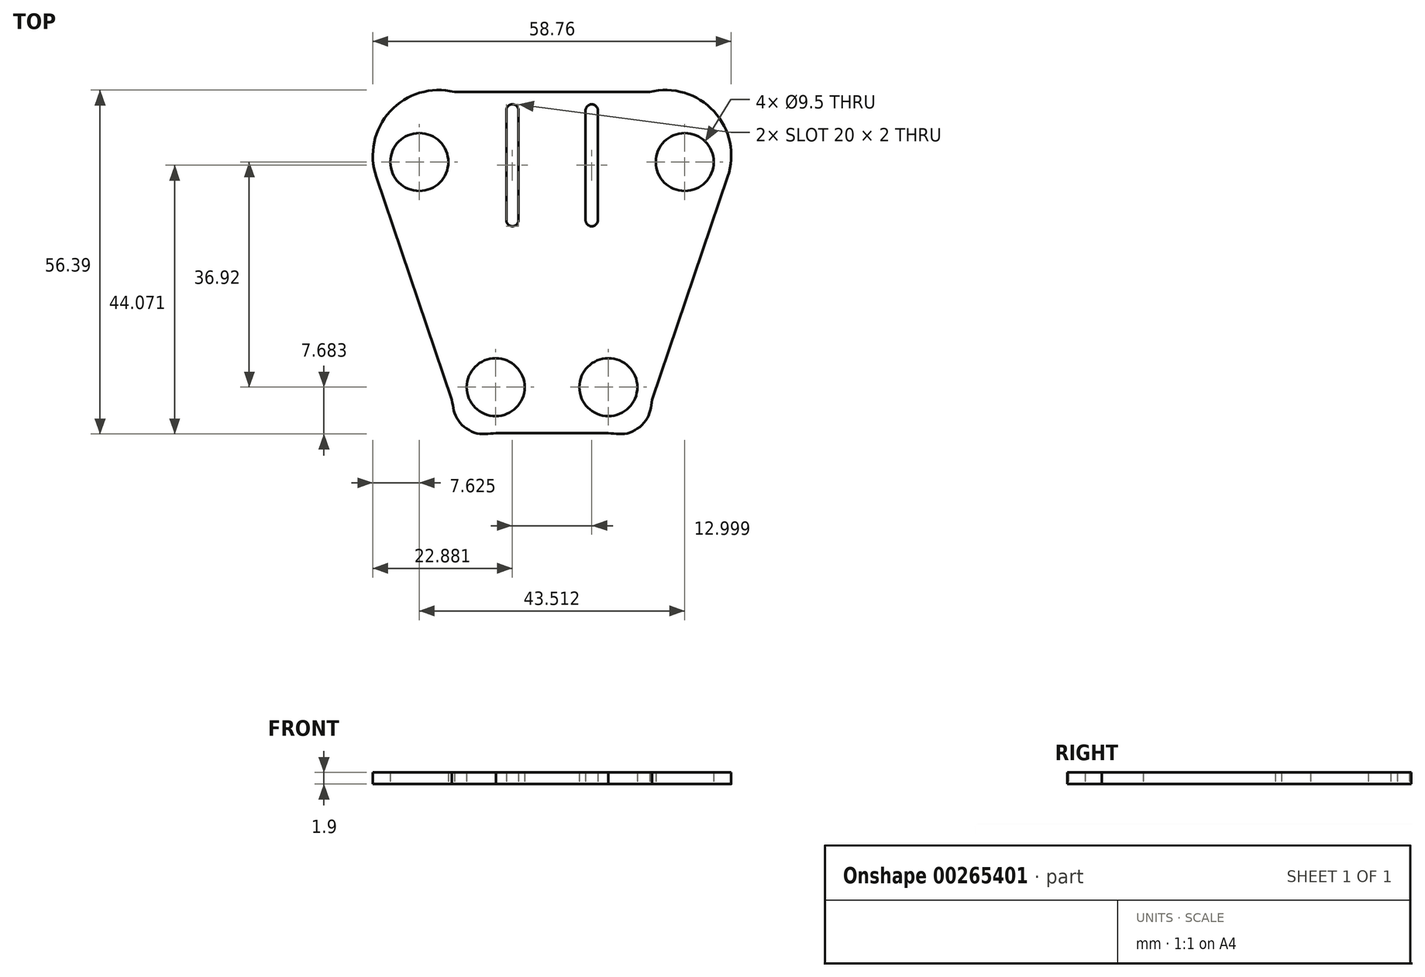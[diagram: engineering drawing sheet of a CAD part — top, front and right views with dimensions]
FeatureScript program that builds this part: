
annotation { "Feature Type Name" : "Feature", "Feature Type Description" : "" }
export const myFeature = defineFeature(function(context is Context, id is Id, definition is map)
    precondition{}
    {
        {
            var Q0;
            Q0=qCreatedBy(makeId("Top.planeOp"),FACE);
            var sketch = newSketch(context, id + "F0", { "sketchPlane" : qUnion([Q0])});
            skEllipse(sketch, "E0", {"center": v(22.76, 23.7) * mm, "majorRadius": 4.75 * mm, "minorRadius": 4.75 * mm, "majorAxis": v(1, 0)});
            skEllipse(sketch, "E1", {"center": v(10.24, -13.22) * mm, "majorRadius": 4.75 * mm, "minorRadius": 4.75 * mm, "majorAxis": v(1, 0)});
            skFitSpline(sketch, "E2", {"points": [v(10.2, -20.72) * mm, v(13.54, -20.72) * mm, v(16.48, -18.5) * mm, v(17.4, -15.28) * mm]});
            skArc(sketch, "E3", {"start": v(29.8, 21.26) * mm, "mid": v(29.86, 21.4) * mm, "end": v(29.9, 21.54) * mm});
            skLineSegment(sketch, "E4", {"start": v(17.4, -15.28) * mm, "end": v(29.8, 21.26) * mm});
            skLineSegment(sketch, "E5", {"start": v(1, -36.13) * mm, "end": v(1, 35.17) * mm, "construction": true});
            skPoint(sketch, "E6.orphan", {"position": v(1, -20.72) * mm});
            skLineSegment(sketch, "E7", {"start": v(1, 35.17) * mm, "end": v(17, 35.17) * mm});
            skArc(sketch, "E8", {"start": v(29.8, 21.26) * mm, "mid": v(27.53, 32.02) * mm, "end": v(17, 35.17) * mm});
            skLineSegment(sketch, "E9.trimOffspring", {"start": v(1, 35.17) * mm, "end": v(1, 47.51) * mm, "construction": true});
            skPoint(sketch, "E10.orphan", {"position": v(22.76, 31.17) * mm});
            skLineSegment(sketch, "E11", {"start": v(10.2, -20.72) * mm, "end": v(1, -20.72) * mm});
            skArc(sketch, "E12.MirrorCS", {"start": v(-27.8, 21.26) * mm, "mid": v(-27.86, 21.4) * mm, "end": v(-27.9, 21.54) * mm});
            skLineSegment(sketch, "E13.MirrorCS", {"start": v(-15.4, -15.28) * mm, "end": v(-27.8, 21.26) * mm});
            skLineSegment(sketch, "E14.MirrorCS", {"start": v(-8.2, -20.72) * mm, "end": v(1, -20.72) * mm});
            skLineSegment(sketch, "E15.MirrorCS", {"start": v(1, 35.17) * mm, "end": v(-15, 35.17) * mm});
            skEllipse(sketch, "E16.MirrorC", {"center": v(-8.23, -13.22) * mm, "majorRadius": 4.75 * mm, "minorRadius": 4.75 * mm, "majorAxis": v(-1, 0)});
            skFitSpline(sketch, "E17.MirrorCS", {"points": [v(-8.2, -20.72) * mm, v(-11.54, -20.72) * mm, v(-14.48, -18.5) * mm, v(-15.4, -15.28) * mm]});
            skEllipse(sketch, "E18.MirrorC", {"center": v(-20.76, 23.7) * mm, "majorRadius": 4.75 * mm, "minorRadius": 4.75 * mm, "majorAxis": v(-1, 0)});
            skPoint(sketch, "E19.MirrorP", {"position": v(-20.76, 31.17) * mm});
            skArc(sketch, "E20.MirrorCS", {"start": v(-27.8, 21.26) * mm, "mid": v(-25.53, 32.02) * mm, "end": v(-15, 35.17) * mm});
            skLineSegment(sketch, "E21", {"start": v(1, 35.17) * mm, "end": v(9, 35.17) * mm});
            skLineSegment(sketch, "E22", {"start": v(7.5, 14.17) * mm, "end": v(6.5, 14.17) * mm, "construction": true});
            skArc(sketch, "E23", {"start": v(-4.5, 32.17) * mm, "mid": v(-5.52, 33.17) * mm, "end": v(-6.5, 32.12) * mm});
            skArc(sketch, "E24", {"start": v(8.5, 32.17) * mm, "mid": v(7.5, 33.17) * mm, "end": v(6.5, 32.17) * mm});
            skArc(sketch, "E25", {"start": v(6.5, 14.17) * mm, "mid": v(7.5, 13.17) * mm, "end": v(8.5, 14.17) * mm});
            skArc(sketch, "E26", {"start": v(-6.5, 14.22) * mm, "mid": v(-5.52, 13.17) * mm, "end": v(-4.5, 14.17) * mm});
            skLineSegment(sketch, "E27", {"start": v(-6.5, 32.22) * mm, "end": v(-6.5, 14.12) * mm});
            skLineSegment(sketch, "E28", {"start": v(-4.5, 32.17) * mm, "end": v(-4.5, 14.17) * mm});
            skLineSegment(sketch, "E29", {"start": v(8.5, 32.17) * mm, "end": v(8.5, 14.17) * mm});
            skLineSegment(sketch, "E30", {"start": v(6.5, 14.17) * mm, "end": v(6.5, 32.17) * mm});
            skLineSegment(sketch, "E31.trimOffspring", {"start": v(-4.5, 14.17) * mm, "end": v(-5.5, 14.17) * mm, "construction": true});
            skSolve(sketch);
        }
        {
            var Q0;
            Q0=makeQuery(id+"F0.imprint","IMPRINT",FACE,{"disambiguationData":[TD([[makeQuery(id+"F0.imprint","IMPRINT",EDGE,{"derivedFrom":sQuery(id+"F0.wireOp",EDGE,"E0")}),-1.0]])]});
            extrude(context, id + "F1", {"entities" : qUnion([Q0]), "depth" : 1.9 * mm});
        }
    });
